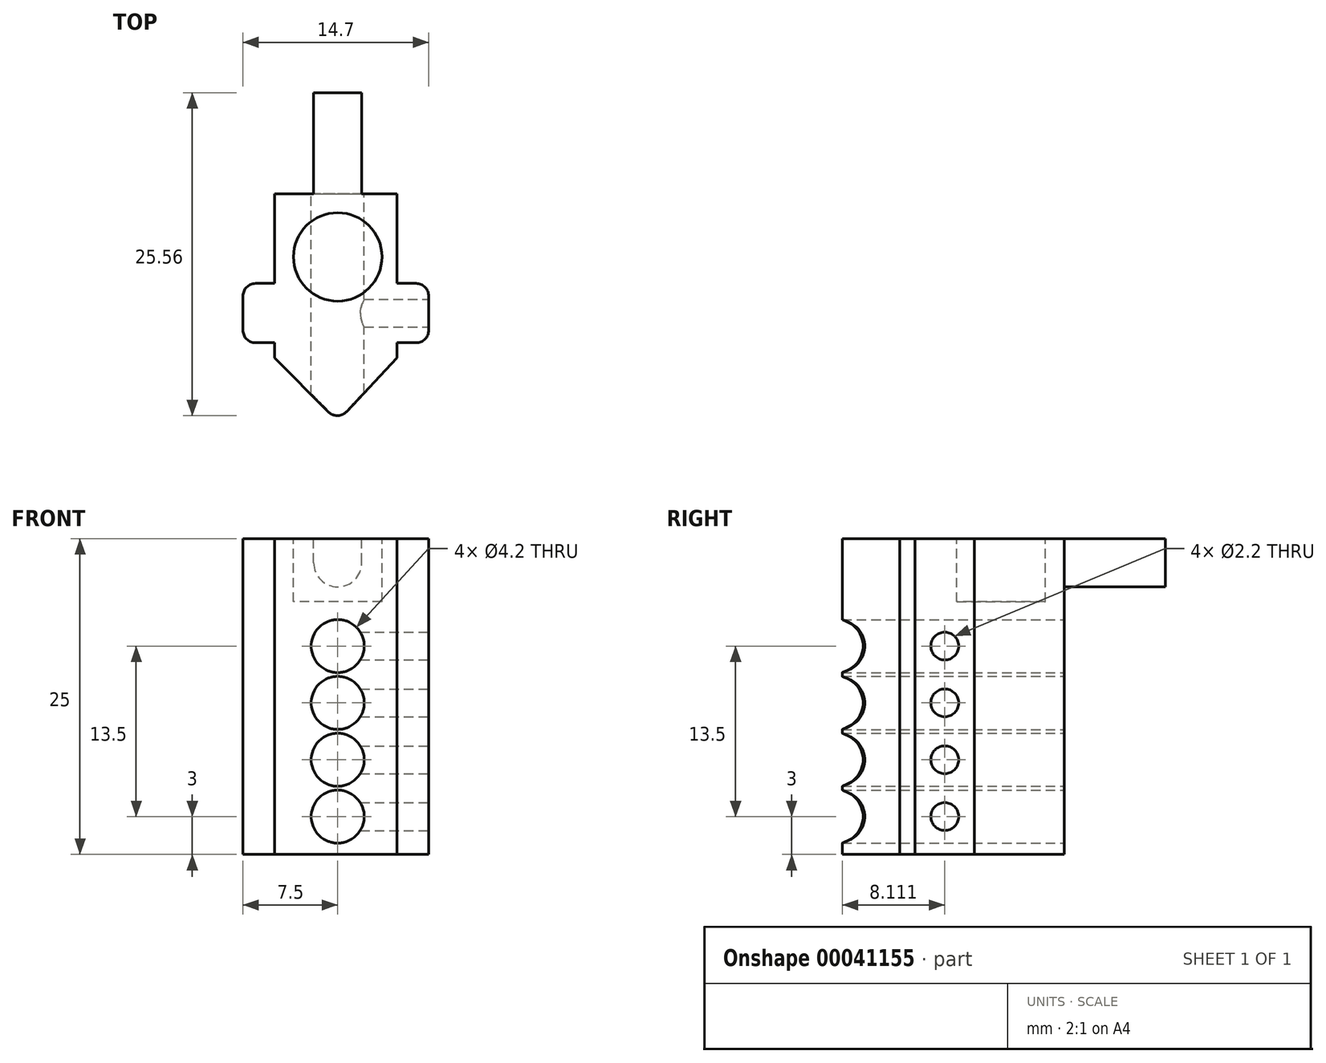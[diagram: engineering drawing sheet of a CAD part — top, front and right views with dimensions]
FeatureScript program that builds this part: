
annotation { "Feature Type Name" : "Feature", "Feature Type Description" : "" }
export const myFeature = defineFeature(function(context is Context, id is Id, definition is map)
    precondition{}
    {
        {
            var Q0;
            Q0=qCreatedBy(makeId("Top.planeOp"),FACE);
            var sketch = newSketch(context, id + "F0", { "sketchPlane" : qUnion([Q0])});
            skLineSegment(sketch, "E0.bottom", {"start": v(-5, 3.37) * mm, "end": v(4.7, 3.37) * mm});
            skLineSegment(sketch, "E0.top", {"start": v(-5, -9.63) * mm, "end": v(4.7, -9.63) * mm});
            skLineSegment(sketch, "E0.left", {"start": v(-5, 3.37) * mm, "end": v(-5, -9.63) * mm});
            skLineSegment(sketch, "E0.right", {"start": v(4.7, 3.37) * mm, "end": v(4.7, -9.63) * mm});
            skLineSegment(sketch, "E1.bottom", {"start": v(7.2, -3.73) * mm, "end": v(-7.5, -3.73) * mm});
            skLineSegment(sketch, "E1.top", {"start": v(7.2, -8.43) * mm, "end": v(-7.5, -8.43) * mm});
            skLineSegment(sketch, "E1.left", {"start": v(7.2, -3.73) * mm, "end": v(7.2, -8.43) * mm});
            skLineSegment(sketch, "E1.right", {"start": v(-7.5, -3.73) * mm, "end": v(-7.5, -8.43) * mm});
            skLineSegment(sketch, "E2", {"start": v(-5, -9.63) * mm, "end": v(0, -14.63) * mm});
            skLineSegment(sketch, "E3", {"start": v(0, -14.63) * mm, "end": v(4.7, -9.63) * mm});
            skSolve(sketch);
        }
        {
            var Q0;
            Q0 = qSketchRegion(id + "F0", true);
            extrude(context, id + "F1", {"entities" : qUnion([Q0]), "depth" : 25 * mm});
        }
        {
            var Q0;
            Q0=makeQuery(id+"F1.opExtrude","SWEPT_EDGE",EDGE,{"disambiguationData":[OSD([sQuery(id+"F0.wireOp",EDGE,"E1.bottom"),sQuery(id+"F0.wireOp",EDGE,"E1.right")])]});
            var Q1;
            Q1=makeQuery(id+"F1.opExtrude","SWEPT_EDGE",EDGE,{"disambiguationData":[OSD([sQuery(id+"F0.wireOp",EDGE,"E1.top"),sQuery(id+"F0.wireOp",EDGE,"E1.right")])]});
            var Q2;
            Q2=makeQuery(id+"F1.opExtrude","SWEPT_EDGE",EDGE,{"disambiguationData":[OSD([sQuery(id+"F0.wireOp",EDGE,"E1.bottom"),sQuery(id+"F0.wireOp",EDGE,"E1.left")])]});
            var Q3;
            Q3=makeQuery(id+"F1.opExtrude","SWEPT_EDGE",EDGE,{"disambiguationData":[OSD([sQuery(id+"F0.wireOp",EDGE,"E1.top"),sQuery(id+"F0.wireOp",EDGE,"E1.left")])]});
            var Q4;
            Q4=makeQuery(id+"F1.opExtrude","SWEPT_EDGE",EDGE,{"disambiguationData":[OSD([sQuery(id+"F0.wireOp",EDGE,"E2"),sQuery(id+"F0.wireOp",EDGE,"E3")])]});
            fillet(context, id + "F2", {"entities" : qUnion([Q0, Q1, Q2, Q3, Q4]), "radius" : 1 * mm, "tangentPropagation" : true, "allowEdgeOverflow" : false});
        }
        {
            var Q0;
            Q0=makeQuery(id+"F1.opExtrude","SWEPT_FACE",FACE,{"disambiguationData":[OSD([sQuery(id+"F0.wireOp",EDGE,"E0.bottom")])]});
            var sketch = newSketch(context, id + "F3", { "sketchPlane" : qUnion([Q0])});
            skPoint(sketch, "E4.startSnap0", {"position": v(-4.7, 12.5) * mm});
            skCircle(sketch, "E5", {"center": v(0, 7.5) * mm, "radius": 2.1 * mm});
            skCircle(sketch, "E6", {"center": v(0, 12) * mm, "radius": 2.1 * mm});
            skCircle(sketch, "E7", {"center": v(0, 3) * mm, "radius": 2.1 * mm});
            skCircle(sketch, "E8", {"center": v(0, 16.5) * mm, "radius": 2.1 * mm});
            skSolve(sketch);
        }
        {
            var Q0;
            Q0 = qSketchRegion(id + "F3", true);
            extrude(context, id + "F4", {"entities" : qUnion([Q0]), "operationType" : NewBodyOperationType.REMOVE, "oppositeDirection" : true, "depth" : 30 * mm});
        }
        {
            var Q0;
            Q0=makeQuery(id+"F1.opExtrude","SWEPT_FACE",FACE,{"disambiguationData":[OSD([sQuery(id+"F0.wireOp",EDGE,"E0.bottom")])]});
            var sketch = newSketch(context, id + "F5", { "sketchPlane" : qUnion([Q0])});
            skCircle(sketch, "E9", {"center": v(0, 23.1) * mm, "radius": 1.9 * mm});
            skLineSegment(sketch, "E10", {"start": v(-1.9, 23.1) * mm, "end": v(-1.9, 25) * mm});
            skLineSegment(sketch, "E11", {"start": v(1.9, 23.1) * mm, "end": v(1.9, 25) * mm});
            skLineSegment(sketch, "E12", {"start": v(-1.9, 25) * mm, "end": v(1.9, 25) * mm});
            skSolve(sketch);
        }
        {
            var Q0;
            Q0 = qSketchRegion(id + "F5", true);
            extrude(context, id + "F6", {"entities" : qUnion([Q0]), "operationType" : NewBodyOperationType.ADD, "depth" : 8 * mm});
        }
        {
            var Q0;
            Q0=makeQuery(id+"F1.opExtrude","CAP_FACE",FACE,{"disambiguationData":[OSD([sQuery(id+"F0.wireOp",EDGE,"E0.bottom"),sQuery(id+"F0.wireOp",EDGE,"E0.left"),sQuery(id+"F0.wireOp",EDGE,"E0.right"),sQuery(id+"F0.wireOp",EDGE,"E1.bottom"),sQuery(id+"F0.wireOp",EDGE,"E1.top"),sQuery(id+"F0.wireOp",EDGE,"E1.left"),sQuery(id+"F0.wireOp",EDGE,"E1.right"),sQuery(id+"F0.wireOp",EDGE,"E2"),sQuery(id+"F0.wireOp",EDGE,"E3")])],"isStart":false});
            var sketch = newSketch(context, id + "F7", { "sketchPlane" : qUnion([Q0])});
            skCircle(sketch, "E13", {"center": v(0, -1.63) * mm, "radius": 3.5 * mm});
            skSolve(sketch);
        }
        {
            var Q0;
            Q0 = qSketchRegion(id + "F7", true);
            extrude(context, id + "F8", {"entities" : qUnion([Q0]), "operationType" : NewBodyOperationType.REMOVE, "oppositeDirection" : true, "depth" : 5 * mm});
        }
        {
            var Q0;
            Q0=makeQuery(id+"F1.opExtrude","SWEPT_FACE",FACE,{"disambiguationData":[OSD([sQuery(id+"F0.wireOp",EDGE,"E1.left")])]});
            var sketch = newSketch(context, id + "F9", { "sketchPlane" : qUnion([Q0])});
            skCircle(sketch, "E14", {"center": v(-6.08, 16.5) * mm, "radius": 1.1 * mm});
            skCircle(sketch, "E15", {"center": v(-6.08, 12) * mm, "radius": 1.1 * mm});
            skCircle(sketch, "E16", {"center": v(-6.08, 7.5) * mm, "radius": 1.1 * mm});
            skCircle(sketch, "E17", {"center": v(-6.08, 3) * mm, "radius": 1.1 * mm});
            skLineSegment(sketch, "E18", {"start": v(-6.08, 25) * mm, "end": v(-6.08, 0) * mm});
            skSolve(sketch);
        }
        {
            var Q0;
            Q0 = qSketchRegion(id + "F9", true);
            extrude(context, id + "F10", {"entities" : qUnion([Q0]), "operationType" : NewBodyOperationType.REMOVE, "oppositeDirection" : true, "depth" : 6 * mm});
        }
    });
